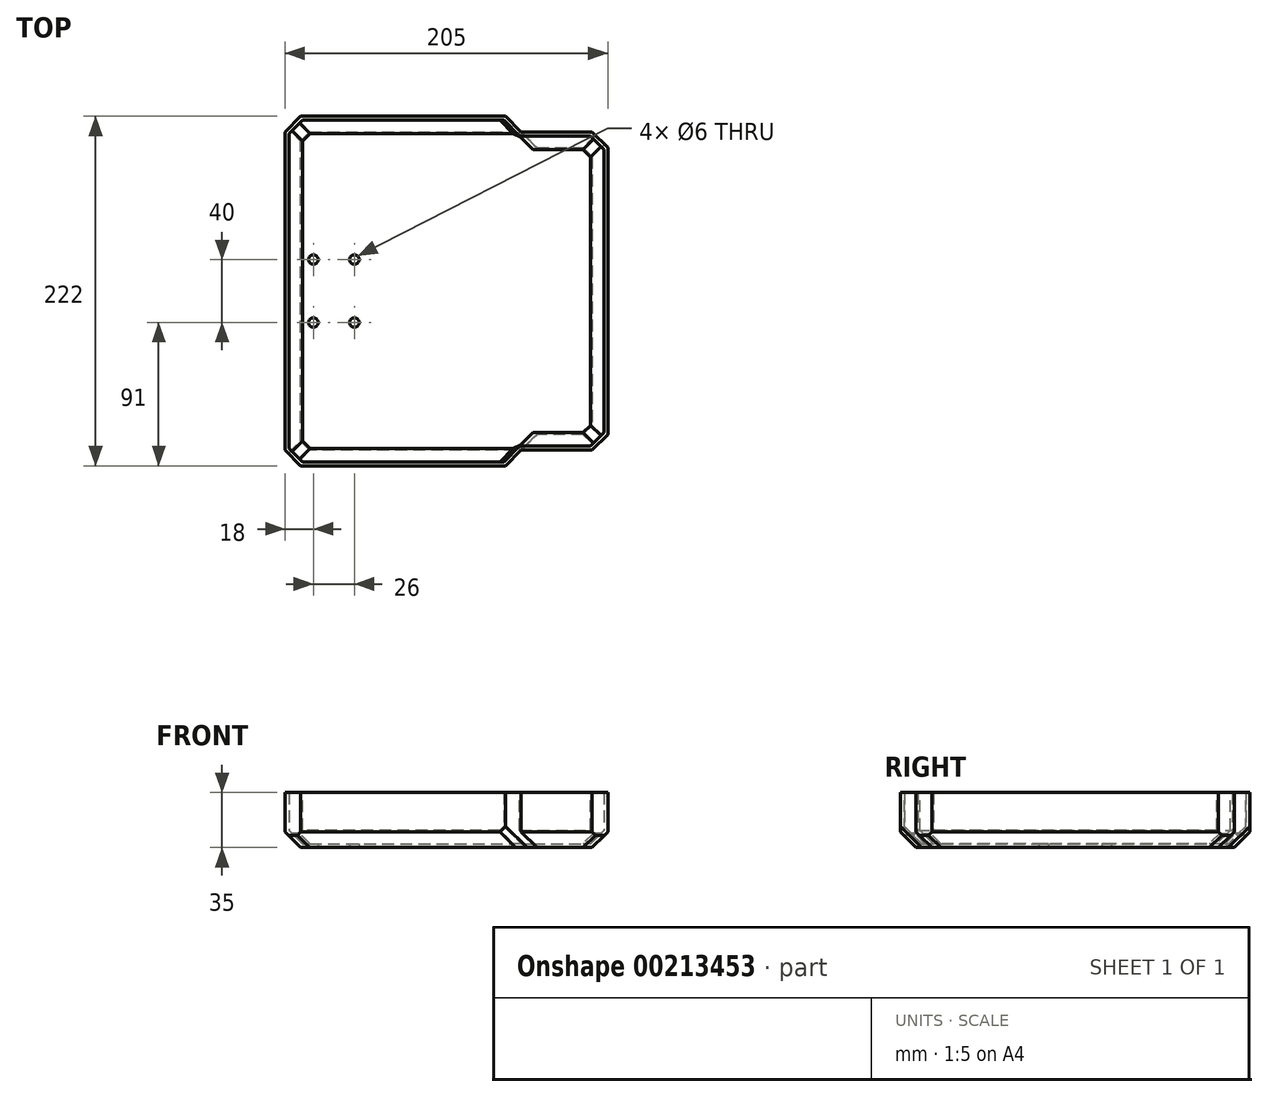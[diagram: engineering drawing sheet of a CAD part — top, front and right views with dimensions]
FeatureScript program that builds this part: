
annotation { "Feature Type Name" : "Feature", "Feature Type Description" : "" }
export const myFeature = defineFeature(function(context is Context, id is Id, definition is map)
    precondition{}
    {
        {
            var Q0;
            Q0=qCreatedBy(makeId("Front.planeOp"),FACE);
            var sketch = newSketch(context, id + "F0", { "sketchPlane" : qUnion([Q0])});
            skLineSegment(sketch, "E0.bottom", {"start": v(10, 0) * mm, "end": v(140, 0) * mm});
            skLineSegment(sketch, "E0.left", {"start": v(0, 10) * mm, "end": v(0, 35) * mm});
            skLineSegment(sketch, "E0.right", {"start": v(150, 10) * mm, "end": v(150, 35) * mm});
            skPoint(sketch, "E1.visualSharp", {"position": v(0, 0) * mm});
            skPoint(sketch, "E2.visualSharp", {"position": v(150, 0) * mm});
            skLineSegment(sketch, "E3", {"start": v(0, 35) * mm, "end": v(150, 35) * mm});
            skLineSegment(sketch, "E4", {"start": v(150, 10) * mm, "end": v(150, 0) * mm});
            skLineSegment(sketch, "E5", {"start": v(140, 0) * mm, "end": v(150, 0) * mm});
            skLineSegment(sketch, "E6", {"start": v(10, 0) * mm, "end": v(0, 0) * mm});
            skLineSegment(sketch, "E7", {"start": v(0, 10) * mm, "end": v(0, 0) * mm});
            skSolve(sketch);
        }
        {
            var Q0;
            Q0=qSketchRegion(id+"F0",true);
            var Q1;
            Q1=qConstructionFilter(qBodyType(qCreatedBy(id+"F0",EDGE),BodyType.WIRE),ConstructionObject.NO);
            extrude(context, id + "F1", {"entities" : qUnion([Q0]), "surfaceEntities" : qUnion([Q1]), "depth" : 222 * mm});
        }
        {
            var Q0;
            Q0=makeQuery(id+"F1.opExtrude","CAP_EDGE",EDGE,{"disambiguationData":[OSD([sQuery(id+"F0.wireOp",EDGE,"E0.left"),sQuery(id+"F0.wireOp",EDGE,"E7")])],"isStart":false});
            var Q1;
            Q1=makeQuery(id+"F1.opExtrude","CAP_EDGE",EDGE,{"disambiguationData":[OSD([sQuery(id+"F0.wireOp",EDGE,"E0.right"),sQuery(id+"F0.wireOp",EDGE,"E4")])],"isStart":false});
            var Q2;
            Q2=makeQuery(id+"F1.opExtrude","CAP_EDGE",EDGE,{"disambiguationData":[OSD([sQuery(id+"F0.wireOp",EDGE,"E0.right"),sQuery(id+"F0.wireOp",EDGE,"E4")])],"isStart":true});
            var Q3;
            Q3=makeQuery(id+"F1.opExtrude","CAP_EDGE",EDGE,{"disambiguationData":[OSD([sQuery(id+"F0.wireOp",EDGE,"E0.left"),sQuery(id+"F0.wireOp",EDGE,"E7")])],"isStart":true});
            chamfer(context, id + "F2", {"entities" : qUnion([Q0, Q1, Q2, Q3]), "width" : 10 * mm, "tangentPropagation" : true});
        }
        {
            var Q0;
            Q0=makeQuery(id+"F1.opExtrude","CAP_EDGE",EDGE,{"disambiguationData":[OSD([sQuery(id+"F0.wireOp",EDGE,"E0.bottom"),sQuery(id+"F0.wireOp",EDGE,"E5"),sQuery(id+"F0.wireOp",EDGE,"E6")])],"isStart":false});
            var Q1;
            Q1=makeQuery(id+"F1.opExtrude","CAP_EDGE",EDGE,{"disambiguationData":[OSD([sQuery(id+"F0.wireOp",EDGE,"E0.bottom"),sQuery(id+"F0.wireOp",EDGE,"E5"),sQuery(id+"F0.wireOp",EDGE,"E6")])],"isStart":true});
            var Q2;
            Q2=makeQuery(id+"F1.opExtrude","SWEPT_EDGE",EDGE,{"disambiguationData":[OSD([sQuery(id+"F0.wireOp",EDGE,"E6"),sQuery(id+"F0.wireOp",EDGE,"E7")])]});
            chamfer(context, id + "F3", {"entities" : qUnion([Q0, Q1, Q2]), "width" : 10 * mm, "tangentPropagation" : true});
        }
        {
            var Q0;
            {var subQ0=sQuery(id+"F0.wireOp",EDGE,"E6");Q0=makeQuery(id+"F3.opChamfer","BLEND_EDGE",EDGE,{"blendedFrom":[makeQuery(id+"F1.opExtrude","SWEPT_EDGE",EDGE,{"disambiguationData":[OSD([subQ0,sQuery(id+"F0.wireOp",EDGE,"E7")])]}),makeQuery(id+"F1.opExtrude","CAP_EDGE",EDGE,{"disambiguationData":[OSD([sQuery(id+"F0.wireOp",EDGE,"E0.bottom"),sQuery(id+"F0.wireOp",EDGE,"E5"),subQ0])],"isStart":false})],"blendedInto":[]});}
            var Q1;
            {var subQ0=sQuery(id+"F0.wireOp",EDGE,"E6");Q1=makeQuery(id+"F3.opChamfer","BLEND_EDGE",EDGE,{"blendedFrom":[makeQuery(id+"F1.opExtrude","SWEPT_EDGE",EDGE,{"disambiguationData":[OSD([subQ0,sQuery(id+"F0.wireOp",EDGE,"E7")])]}),makeQuery(id+"F1.opExtrude","CAP_EDGE",EDGE,{"disambiguationData":[OSD([sQuery(id+"F0.wireOp",EDGE,"E0.bottom"),sQuery(id+"F0.wireOp",EDGE,"E5"),subQ0])],"isStart":true})],"blendedInto":[]});}
            chamfer(context, id + "F4", {"entities" : qUnion([Q0, Q1]), "width" : 8 * mm, "tangentPropagation" : true});
        }
        {
            var Q0;
            Q0=makeQuery(id+"F1.opExtrude","SWEPT_FACE",FACE,{"disambiguationData":[OSD([sQuery(id+"F0.wireOp",EDGE,"E0.bottom")])]});
            var sketch = newSketch(context, id + "F5", { "sketchPlane" : qUnion([Q0])});
            skCircle(sketch, "E8", {"center": v(44, 131) * mm, "radius": 3 * mm});
            skCircle(sketch, "E9", {"center": v(18, 131) * mm, "radius": 3 * mm});
            skCircle(sketch, "E10", {"center": v(44, 91) * mm, "radius": 3 * mm});
            skCircle(sketch, "E11", {"center": v(18, 91) * mm, "radius": 3 * mm});
            skSolve(sketch);
        }
        {
            var Q0;
            Q0=makeQuery(id+"F1.opExtrude","SWEPT_FACE",FACE,{"disambiguationData":[OSD([sQuery(id+"F0.wireOp",EDGE,"E0.right"),sQuery(id+"F0.wireOp",EDGE,"E4")])]});
            var sketch = newSketch(context, id + "F6", { "sketchPlane" : qUnion([Q0])});
            skLineSegment(sketch, "E12.bottom", {"start": v(-10, 35) * mm, "end": v(-212, 35) * mm});
            skLineSegment(sketch, "E12.top", {"start": v(-10, 0) * mm, "end": v(-212, 0) * mm});
            skLineSegment(sketch, "E12.left", {"start": v(-10, 35) * mm, "end": v(-10, 0) * mm});
            skLineSegment(sketch, "E12.right", {"start": v(-212, 35) * mm, "end": v(-212, 0) * mm});
            skSolve(sketch);
        }
        {
            var Q0;
            Q0 = qSketchRegion(id + "F6", true);
            extrude(context, id + "F7", {"entities" : qUnion([Q0]), "operationType" : NewBodyOperationType.ADD, "depth" : 55 * mm});
        }
        {
            var Q0;
            Q0=makeQuery(id+"F7.opExtrude","CAP_EDGE",EDGE,{"disambiguationData":[OSD([sQuery(id+"F6.wireOp",EDGE,"E12.top")])],"isStart":false});
            var Q1;
            Q1=makeQuery(id+"F7.opExtrude","SWEPT_EDGE",EDGE,{"disambiguationData":[OSD([sQuery(id+"F6.wireOp",EDGE,"E12.top"),sQuery(id+"F6.wireOp",EDGE,"E12.right")])]});
            var Q2;
            Q2=makeQuery(id+"F7.opExtrude","SWEPT_EDGE",EDGE,{"disambiguationData":[OSD([sQuery(id+"F6.wireOp",EDGE,"E12.top"),sQuery(id+"F6.wireOp",EDGE,"E12.left")])]});
            chamfer(context, id + "F8", {"entities" : qUnion([Q0, Q1, Q2]), "width" : 10 * mm, "tangentPropagation" : true});
        }
        {
            var Q0;
            Q0=makeQuery(id+"F7.opExtrude","CAP_EDGE",EDGE,{"disambiguationData":[OSD([sQuery(id+"F6.wireOp",EDGE,"E12.right")])],"isStart":false});
            var Q1;
            Q1=makeQuery(id+"F7.opExtrude","CAP_EDGE",EDGE,{"disambiguationData":[OSD([sQuery(id+"F6.wireOp",EDGE,"E12.left")])],"isStart":false});
            chamfer(context, id + "F9", {"entities" : qUnion([Q0, Q1]), "width" : 10 * mm, "tangentPropagation" : true});
        }
        {
            var Q0;
            {var subQ0=sQuery(id+"F0.wireOp",EDGE,"E4");var subQ1=sQuery(id+"F0.wireOp",EDGE,"E0.right");Q0=makeQuery(id+"F3.opChamfer","BLEND_EDGE",EDGE,{"blendedFrom":[makeQuery(id+"F1.opExtrude","CAP_EDGE",EDGE,{"disambiguationData":[OSD([sQuery(id+"F0.wireOp",EDGE,"E0.bottom"),sQuery(id+"F0.wireOp",EDGE,"E5"),sQuery(id+"F0.wireOp",EDGE,"E6")])],"isStart":false}),makeQuery(id+"F2.opChamfer","BLEND_FACE",FACE,{"disambiguationData":[OSD([subQ1,subQ0]),TDD([makeQuery(id+"F1.opExtrude","CAP_EDGE",EDGE,{"disambiguationData":[OSD([subQ1,subQ0])],"isStart":false})])]})],"blendedInto":[makeQuery(id+"F2.opChamfer","BLEND_FACE",FACE,{"disambiguationData":[OSD([subQ1,subQ0]),TDD([makeQuery(id+"F1.opExtrude","CAP_EDGE",EDGE,{"disambiguationData":[OSD([subQ1,subQ0])],"isStart":false})])]})]});}
            var Q1;
            {var subQ0=sQuery(id+"F0.wireOp",EDGE,"E4");var subQ1=sQuery(id+"F0.wireOp",EDGE,"E0.right");Q1=makeQuery(id+"F3.opChamfer","BLEND_EDGE",EDGE,{"blendedFrom":[makeQuery(id+"F1.opExtrude","CAP_EDGE",EDGE,{"disambiguationData":[OSD([sQuery(id+"F0.wireOp",EDGE,"E0.bottom"),sQuery(id+"F0.wireOp",EDGE,"E5"),sQuery(id+"F0.wireOp",EDGE,"E6")])],"isStart":true}),makeQuery(id+"F2.opChamfer","BLEND_FACE",FACE,{"disambiguationData":[OSD([subQ1,subQ0]),TDD([makeQuery(id+"F1.opExtrude","CAP_EDGE",EDGE,{"disambiguationData":[OSD([subQ1,subQ0])],"isStart":true})])]})],"blendedInto":[makeQuery(id+"F2.opChamfer","BLEND_FACE",FACE,{"disambiguationData":[OSD([subQ1,subQ0]),TDD([makeQuery(id+"F1.opExtrude","CAP_EDGE",EDGE,{"disambiguationData":[OSD([subQ1,subQ0])],"isStart":true})])]})]});}
            chamfer(context, id + "F10", {"entities" : qUnion([Q0, Q1]), "width" : 5 * mm, "tangentPropagation" : true});
        }
        {
            var Q0;
            {var subQ0=sQuery(id+"F6.wireOp",EDGE,"E12.top");Q0=makeQuery(id+"F8.opChamfer","BLEND_EDGE",EDGE,{"blendedFrom":[makeQuery(id+"F7.opExtrude","SWEPT_EDGE",EDGE,{"disambiguationData":[OSD([subQ0,sQuery(id+"F6.wireOp",EDGE,"E12.left")])]}),makeQuery(id+"F7.opExtrude","CAP_EDGE",EDGE,{"disambiguationData":[OSD([subQ0])],"isStart":false})],"blendedInto":[]});}
            var Q1;
            {var subQ0=sQuery(id+"F6.wireOp",EDGE,"E12.top");Q1=makeQuery(id+"F8.opChamfer","BLEND_EDGE",EDGE,{"blendedFrom":[makeQuery(id+"F7.opExtrude","SWEPT_EDGE",EDGE,{"disambiguationData":[OSD([subQ0,sQuery(id+"F6.wireOp",EDGE,"E12.right")])]}),makeQuery(id+"F7.opExtrude","CAP_EDGE",EDGE,{"disambiguationData":[OSD([subQ0])],"isStart":false})],"blendedInto":[]});}
            chamfer(context, id + "F11", {"entities" : qUnion([Q0, Q1]), "width" : 8 * mm, "tangentPropagation" : true});
        }
        {
            var Q0;
            Q0=makeQuery(id+"F1.opExtrude","SWEPT_FACE",FACE,{"disambiguationData":[OSD([sQuery(id+"F0.wireOp",EDGE,"E3")])]});
            shell(context, id + "F12", {"entities" : qUnion([Q0]), "thickness" : 2.5 * mm});
        }
        {
            var Q0;
            Q0=makeQuery(id+"F5.imprint","IMPRINT",FACE,{"disambiguationData":[TD([[makeQuery(id+"F5.imprint","IMPRINT",EDGE,{"derivedFrom":sQuery(id+"F5.wireOp",EDGE,"E9")}),1.0]])]});
            var Q1;
            Q1=makeQuery(id+"F5.imprint","IMPRINT",FACE,{"disambiguationData":[TD([[makeQuery(id+"F5.imprint","IMPRINT",EDGE,{"derivedFrom":sQuery(id+"F5.wireOp",EDGE,"E8")}),1.0]])]});
            var Q2;
            Q2=makeQuery(id+"F5.imprint","IMPRINT",FACE,{"disambiguationData":[TD([[makeQuery(id+"F5.imprint","IMPRINT",EDGE,{"derivedFrom":sQuery(id+"F5.wireOp",EDGE,"E10")}),1.0]])]});
            var Q3;
            Q3=makeQuery(id+"F5.imprint","IMPRINT",FACE,{"disambiguationData":[TD([[makeQuery(id+"F5.imprint","IMPRINT",EDGE,{"derivedFrom":sQuery(id+"F5.wireOp",EDGE,"E11")}),1.0]])]});
            extrude(context, id + "F13", {"entities" : qUnion([Q0, Q1, Q2, Q3]), "operationType" : NewBodyOperationType.REMOVE, "endBound" : BoundingType.THROUGH_ALL, "oppositeDirection" : true, "depth" : 25 * mm});
        }
    });
